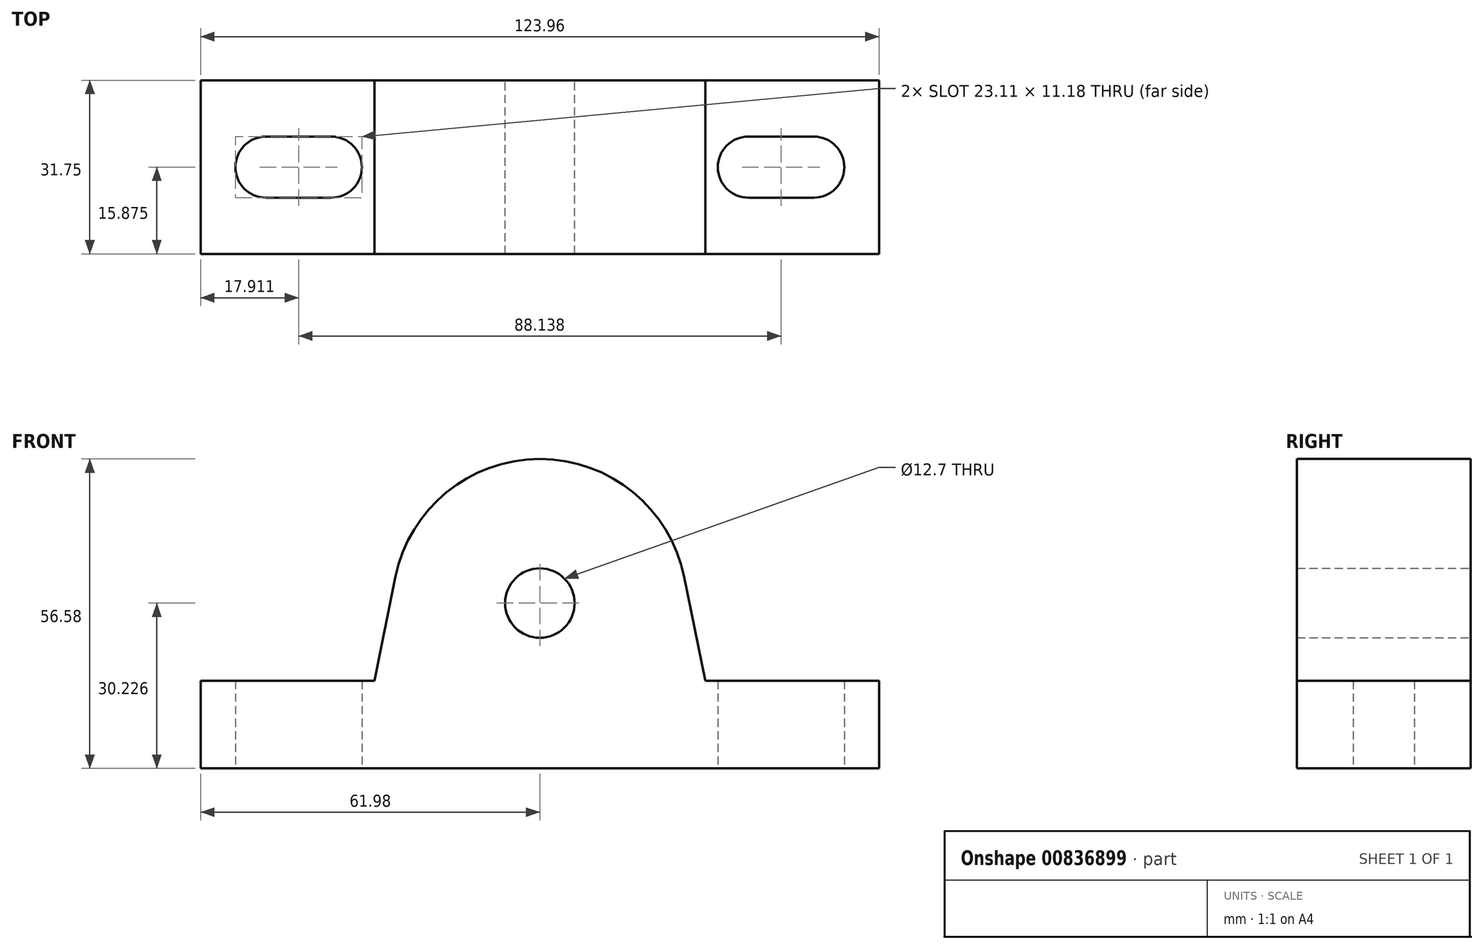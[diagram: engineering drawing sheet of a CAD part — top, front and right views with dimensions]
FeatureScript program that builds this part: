
annotation { "Feature Type Name" : "Feature", "Feature Type Description" : "" }
export const myFeature = defineFeature(function(context is Context, id is Id, definition is map)
    precondition{}
    {
        {
            var Q0;
            Q0=qCreatedBy(makeId("Front.planeOp"),FACE);
            var sketch = newSketch(context, id + "F0", { "sketchPlane" : qUnion([Q0])});
            skLineSegment(sketch, "E0", {"start": v(-61.98, 0) * mm, "end": v(61.98, 0) * mm});
            skLineSegment(sketch, "E1", {"start": v(-61.98, 0) * mm, "end": v(-61.98, 16) * mm});
            skLineSegment(sketch, "E2", {"start": v(-61.98, 16) * mm, "end": v(-30.23, 16) * mm});
            skLineSegment(sketch, "E3", {"start": v(61.98, 0) * mm, "end": v(61.98, 16) * mm});
            skLineSegment(sketch, "E4", {"start": v(61.98, 16) * mm, "end": v(30.23, 16) * mm});
            skArc(sketch, "E5", {"start": v(26.4, 34.99) * mm, "mid": v(0, 56.58) * mm, "end": v(-26.4, 34.99) * mm});
            skLineSegment(sketch, "E6", {"start": v(-30.23, 16) * mm, "end": v(-26.4, 34.99) * mm});
            skLineSegment(sketch, "E7", {"start": v(26.4, 34.99) * mm, "end": v(30.23, 16) * mm});
            skCircle(sketch, "E8", {"center": v(0, 30.23) * mm, "radius": 6.35 * mm});
            skPoint(sketch, "E8.centerSnap0", {"position": v(0, 56.58) * mm});
            skSolve(sketch);
        }
        {
            var Q0;
            Q0 = qSketchRegion(id + "F0", true);
            extrude(context, id + "F1", {"entities" : qUnion([Q0]), "depth" : 31.75 * mm, "offsetDistance" : 25.4 * mm});
        }
        {
            var Q0;
            Q0=makeQuery(id+"F1.opExtrude","SWEPT_FACE",FACE,{"disambiguationData":[OSD([sQuery(id+"F0.wireOp",EDGE,"E0")])]});
            var sketch = newSketch(context, id + "F2", { "sketchPlane" : qUnion([Q0])});
            skArc(sketch, "E9", {"start": v(-50.04, 21.46) * mm, "mid": v(-55.63, 15.88) * mm, "end": v(-50.04, 10.29) * mm});
            skArc(sketch, "E10", {"start": v(-38.1, 10.29) * mm, "mid": v(-32.51, 15.88) * mm, "end": v(-38.1, 21.46) * mm});
            skArc(sketch, "E11", {"start": v(38.1, 21.46) * mm, "mid": v(32.51, 15.87) * mm, "end": v(38.1, 10.29) * mm});
            skArc(sketch, "E12", {"start": v(50.04, 10.29) * mm, "mid": v(55.63, 15.88) * mm, "end": v(50.04, 21.46) * mm});
            skLineSegment(sketch, "E13", {"start": v(-50.04, 15.88) * mm, "end": v(-38.1, 15.88) * mm, "construction": true});
            skLineSegment(sketch, "E14", {"start": v(38.1, 15.88) * mm, "end": v(50.04, 15.88) * mm, "construction": true});
            skLineSegment(sketch, "E15", {"start": v(-38.1, 15.88) * mm, "end": v(38.1, 15.88) * mm, "construction": true});
            skLineSegment(sketch, "E16", {"start": v(-50.04, 21.46) * mm, "end": v(-38.1, 21.46) * mm});
            skLineSegment(sketch, "E17", {"start": v(-38.1, 10.29) * mm, "end": v(-50.04, 10.29) * mm});
            skLineSegment(sketch, "E18", {"start": v(38.1, 21.46) * mm, "end": v(50.04, 21.46) * mm});
            skLineSegment(sketch, "E19", {"start": v(50.04, 10.29) * mm, "end": v(38.1, 10.29) * mm});
            skSolve(sketch);
        }
        {
            var Q0;
            Q0 = qSketchRegion(id + "F2", true);
            extrude(context, id + "F3", {"entities" : qUnion([Q0]), "operationType" : NewBodyOperationType.REMOVE, "oppositeDirection" : true, "depth" : 127 * mm, "offsetDistance" : 25.4 * mm});
        }
    });
